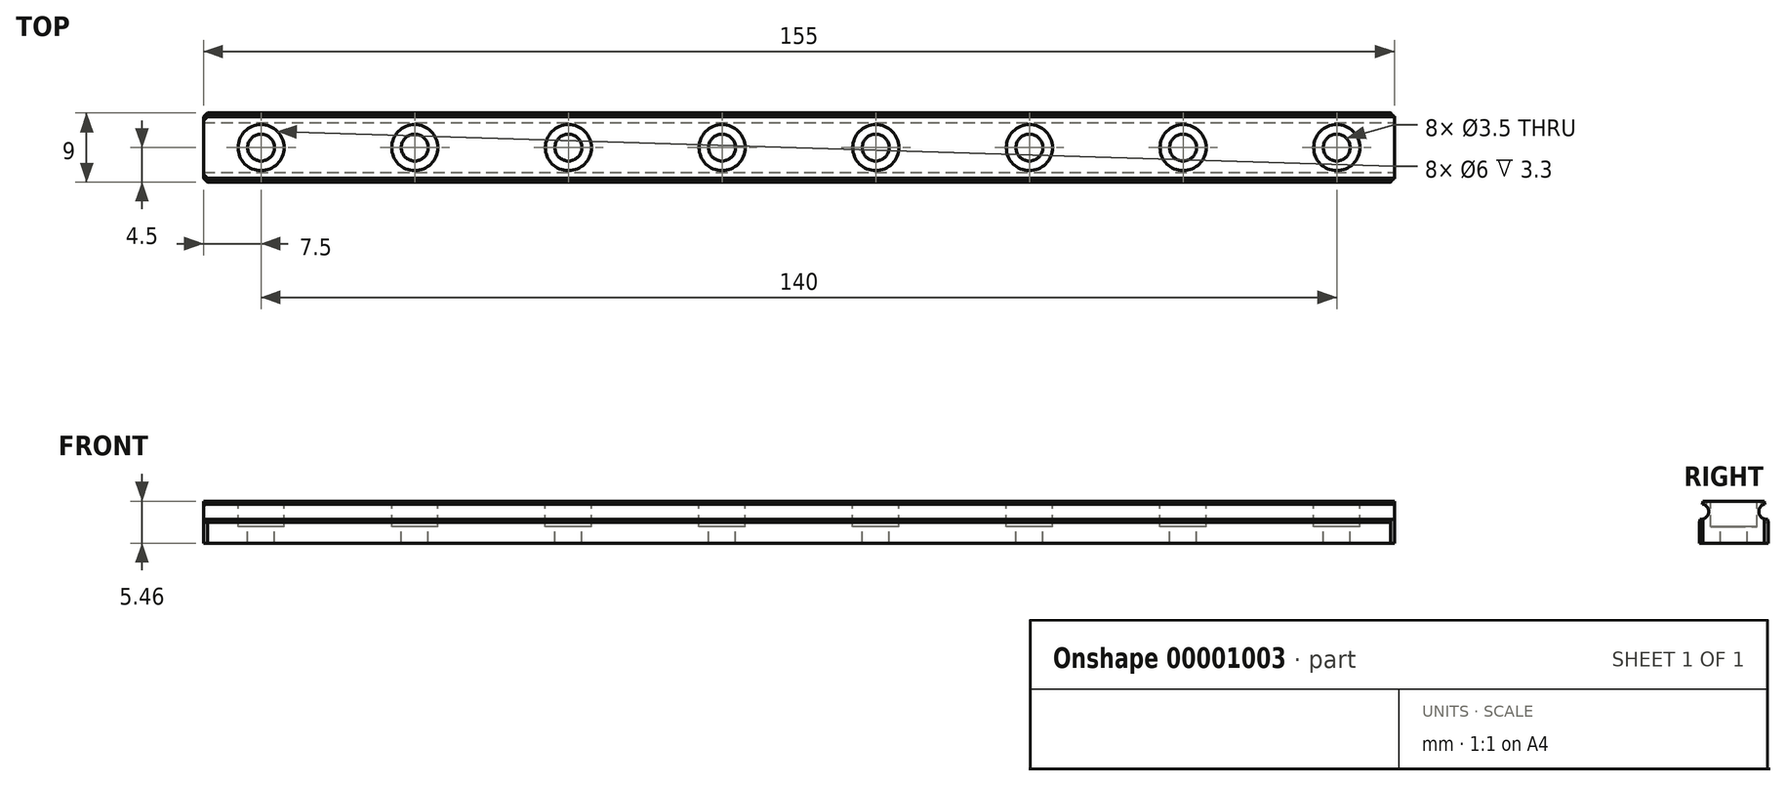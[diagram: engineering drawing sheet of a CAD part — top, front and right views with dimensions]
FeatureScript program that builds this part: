
annotation { "Feature Type Name" : "Feature", "Feature Type Description" : "" }
export const myFeature = defineFeature(function(context is Context, id is Id, definition is map)
    precondition{}
    {
        {
            var Q0;
            Q0=qCreatedBy(makeId("Top.planeOp"),FACE);
            var sketch = newSketch(context, id + "F0", { "sketchPlane" : qUnion([Q0])});
            skLineSegment(sketch, "E0.bottom", {"start": v(77.5, -4.5) * mm, "end": v(-77.5, -4.5) * mm});
            skLineSegment(sketch, "E0.top", {"start": v(77.5, 4.5) * mm, "end": v(-77.5, 4.5) * mm});
            skLineSegment(sketch, "E0.left", {"start": v(77.5, -4.5) * mm, "end": v(77.5, 4.5) * mm});
            skLineSegment(sketch, "E0.right", {"start": v(-77.5, -4.5) * mm, "end": v(-77.5, 4.5) * mm});
            skCircle(sketch, "E1", {"center": v(-10, 0) * mm, "radius": 1.75 * mm});
            skCircle(sketch, "E2", {"center": v(10, 0) * mm, "radius": 1.75 * mm});
            skCircle(sketch, "E3", {"center": v(30, 0) * mm, "radius": 1.75 * mm});
            skCircle(sketch, "E4", {"center": v(-30, 0) * mm, "radius": 1.75 * mm});
            skCircle(sketch, "E5", {"center": v(-50, 0) * mm, "radius": 1.75 * mm});
            skCircle(sketch, "E6", {"center": v(30, 0) * mm, "radius": 3 * mm});
            skCircle(sketch, "E7", {"center": v(10, 0) * mm, "radius": 3 * mm});
            skCircle(sketch, "E8", {"center": v(-10, 0) * mm, "radius": 3 * mm});
            skCircle(sketch, "E9", {"center": v(-30, 0) * mm, "radius": 3 * mm});
            skCircle(sketch, "E10", {"center": v(-50, 0) * mm, "radius": 3 * mm});
            skCircle(sketch, "E11", {"center": v(50, 0) * mm, "radius": 1.75 * mm});
            skCircle(sketch, "E12", {"center": v(50, 0) * mm, "radius": 3 * mm});
            skCircle(sketch, "E13", {"center": v(-70, 0) * mm, "radius": 1.75 * mm});
            skCircle(sketch, "E14", {"center": v(-70, 0) * mm, "radius": 3 * mm});
            skCircle(sketch, "E15", {"center": v(70, 0) * mm, "radius": 1.75 * mm});
            skCircle(sketch, "E16", {"center": v(70, 0) * mm, "radius": 3 * mm});
            skSolve(sketch);
        }
        {
            var Q0;
            Q0=makeQuery(id+"F0.imprint","IMPRINT",FACE,{"disambiguationData":[TD([[makeQuery(id+"F0.imprint","IMPRINT",EDGE,{"derivedFrom":sQuery(id+"F0.wireOp",EDGE,"E0.bottom")}),-1.0]])]});
            var Q1;
            Q1=makeQuery(id+"F0.imprint","IMPRINT",FACE,{"disambiguationData":[TD([[makeQuery(id+"F0.imprint","IMPRINT",EDGE,{"derivedFrom":sQuery(id+"F0.wireOp",EDGE,"E1")}),-1.0]])]});
            var Q2;
            Q2=makeQuery(id+"F0.imprint","IMPRINT",FACE,{"disambiguationData":[TD([[makeQuery(id+"F0.imprint","IMPRINT",EDGE,{"derivedFrom":sQuery(id+"F0.wireOp",EDGE,"E2")}),-1.0]])]});
            var Q3;
            Q3=makeQuery(id+"F0.imprint","IMPRINT",FACE,{"disambiguationData":[TD([[makeQuery(id+"F0.imprint","IMPRINT",EDGE,{"derivedFrom":sQuery(id+"F0.wireOp",EDGE,"E3")}),-1.0]])]});
            var Q4;
            Q4=makeQuery(id+"F0.imprint","IMPRINT",FACE,{"disambiguationData":[TD([[makeQuery(id+"F0.imprint","IMPRINT",EDGE,{"derivedFrom":sQuery(id+"F0.wireOp",EDGE,"E4")}),-1.0]])]});
            var Q5;
            Q5=makeQuery(id+"F0.imprint","IMPRINT",FACE,{"disambiguationData":[TD([[makeQuery(id+"F0.imprint","IMPRINT",EDGE,{"derivedFrom":sQuery(id+"F0.wireOp",EDGE,"E5")}),-1.0]])]});
            var Q6;
            Q6=makeQuery(id+"F0.imprint","IMPRINT",FACE,{"disambiguationData":[TD([[makeQuery(id+"F0.imprint","IMPRINT",EDGE,{"derivedFrom":sQuery(id+"F0.wireOp",EDGE,"E13")}),-1.0]])]});
            var Q7;
            Q7=makeQuery(id+"F0.imprint","IMPRINT",FACE,{"disambiguationData":[TD([[makeQuery(id+"F0.imprint","IMPRINT",EDGE,{"derivedFrom":sQuery(id+"F0.wireOp",EDGE,"E11")}),-1.0]])]});
            var Q8;
            Q8=makeQuery(id+"F0.imprint","IMPRINT",FACE,{"disambiguationData":[TD([[makeQuery(id+"F0.imprint","IMPRINT",EDGE,{"derivedFrom":sQuery(id+"F0.wireOp",EDGE,"E15")}),-1.0]])]});
            extrude(context, id + "F1", {"entities" : qUnion([Q0, Q1, Q2, Q3, Q4, Q5, Q6, Q7, Q8]), "oppositeDirection" : true, "depth" : 5.46 * mm});
        }
        {
            var Q0;
            Q0=makeQuery(id+"F0.imprint","IMPRINT",FACE,{"disambiguationData":[TD([[makeQuery(id+"F0.imprint","IMPRINT",EDGE,{"derivedFrom":sQuery(id+"F0.wireOp",EDGE,"E13")}),-1.0]])]});
            var Q1;
            Q1=makeQuery(id+"F0.imprint","IMPRINT",FACE,{"disambiguationData":[TD([[makeQuery(id+"F0.imprint","IMPRINT",EDGE,{"derivedFrom":sQuery(id+"F0.wireOp",EDGE,"E5")}),-1.0]])]});
            var Q2;
            Q2=makeQuery(id+"F0.imprint","IMPRINT",FACE,{"disambiguationData":[TD([[makeQuery(id+"F0.imprint","IMPRINT",EDGE,{"derivedFrom":sQuery(id+"F0.wireOp",EDGE,"E4")}),-1.0]])]});
            var Q3;
            Q3=makeQuery(id+"F0.imprint","IMPRINT",FACE,{"disambiguationData":[TD([[makeQuery(id+"F0.imprint","IMPRINT",EDGE,{"derivedFrom":sQuery(id+"F0.wireOp",EDGE,"E1")}),-1.0]])]});
            var Q4;
            Q4=makeQuery(id+"F0.imprint","IMPRINT",FACE,{"disambiguationData":[TD([[makeQuery(id+"F0.imprint","IMPRINT",EDGE,{"derivedFrom":sQuery(id+"F0.wireOp",EDGE,"E2")}),-1.0]])]});
            var Q5;
            Q5=makeQuery(id+"F0.imprint","IMPRINT",FACE,{"disambiguationData":[TD([[makeQuery(id+"F0.imprint","IMPRINT",EDGE,{"derivedFrom":sQuery(id+"F0.wireOp",EDGE,"E3")}),-1.0]])]});
            var Q6;
            Q6=makeQuery(id+"F0.imprint","IMPRINT",FACE,{"disambiguationData":[TD([[makeQuery(id+"F0.imprint","IMPRINT",EDGE,{"derivedFrom":sQuery(id+"F0.wireOp",EDGE,"E11")}),-1.0]])]});
            var Q7;
            Q7=makeQuery(id+"F0.imprint","IMPRINT",FACE,{"disambiguationData":[TD([[makeQuery(id+"F0.imprint","IMPRINT",EDGE,{"derivedFrom":sQuery(id+"F0.wireOp",EDGE,"E15")}),-1.0]])]});
            extrude(context, id + "F2", {"entities" : qUnion([Q0, Q1, Q2, Q3, Q4, Q5, Q6, Q7]), "operationType" : NewBodyOperationType.REMOVE, "oppositeDirection" : true, "depth" : 3.3 * mm});
        }
        {
            var Q0;
            Q0=makeQuery(id+"F1.opExtrude","SWEPT_FACE",FACE,{"disambiguationData":[OSD([sQuery(id+"F0.wireOp",EDGE,"E0.left")])]});
            var sketch = newSketch(context, id + "F3", { "sketchPlane" : qUnion([Q0])});
            skLineSegment(sketch, "E17", {"start": v(-4, 0) * mm, "end": v(-4.07, -0.38) * mm});
            skLineSegment(sketch, "E18", {"start": v(4.5, -2.73) * mm, "end": v(4.43, -2.35) * mm});
            skArc(sketch, "E19", {"start": v(-4.43, -2.35) * mm, "mid": v(-3.27, -1.55) * mm, "end": v(-4.07, -0.38) * mm});
            skArc(sketch, "E20", {"start": v(4.07, -0.38) * mm, "mid": v(3.27, -1.55) * mm, "end": v(4.43, -2.35) * mm});
            skLineSegment(sketch, "E21.trimOffspring", {"start": v(-4.43, -2.35) * mm, "end": v(-4.5, -2.73) * mm});
            skLineSegment(sketch, "E22.trimOffspring", {"start": v(4.07, -0.38) * mm, "end": v(4, 0) * mm});
            skLineSegment(sketch, "E23", {"start": v(-4, 0) * mm, "end": v(-4.5, 0) * mm});
            skLineSegment(sketch, "E24", {"start": v(-4.5, 0) * mm, "end": v(-4.5, -2.73) * mm});
            skLineSegment(sketch, "E25", {"start": v(4, 0) * mm, "end": v(4.5, 0) * mm});
            skLineSegment(sketch, "E26", {"start": v(4.5, 0) * mm, "end": v(4.5, -2.73) * mm});
            skSolve(sketch);
        }
        {
            var Q0;
            {Q0=qUnion([makeQuery(id+"F3.imprint","IMPRINT",FACE,{"disambiguationData":[TD([[makeQuery(id+"F3.imprint","IMPRINT",EDGE,{"derivedFrom":sQuery(id+"F3.wireOp",EDGE,"E17")}),-1.0]])]}),makeQuery(id+"F3.imprint","IMPRINT",FACE,{"disambiguationData":[TD([[makeQuery(id+"F3.imprint","IMPRINT",EDGE,{"derivedFrom":sQuery(id+"F3.wireOp",EDGE,"E18")}),-1.0]])]})]);}
            extrude(context, id + "F4", {"entities" : qUnion([Q0]), "operationType" : NewBodyOperationType.REMOVE, "endBound" : BoundingType.THROUGH_ALL, "oppositeDirection" : true, "depth" : 25.4 * mm});
        }
        {
            var Q0;
            Q0=makeQuery(id+"F4.boolean.opBoolean","COPY",EDGE,{"derivedFrom":makeQuery(id+"F4.opExtrude","CAP_EDGE",EDGE,{"disambiguationData":[OSD([sQuery(id+"F3.wireOp",EDGE,"E22.trimOffspring")])],"isStart":true})});
            var Q1;
            Q1=makeQuery(id+"F4.boolean.opBoolean","COPY",EDGE,{"derivedFrom":makeQuery(id+"F4.opExtrude","CAP_EDGE",EDGE,{"disambiguationData":[OSD([sQuery(id+"F3.wireOp",EDGE,"E18")])],"isStart":true})});
            var Q2;
            Q2=makeQuery(id+"F1.opExtrude","SWEPT_EDGE",EDGE,{"disambiguationData":[OSD([sQuery(id+"F0.wireOp",EDGE,"E0.top"),sQuery(id+"F0.wireOp",EDGE,"E0.left")])]});
            var Q3;
            Q3=makeQuery(id+"F1.opExtrude","SWEPT_EDGE",EDGE,{"disambiguationData":[OSD([sQuery(id+"F0.wireOp",EDGE,"E0.bottom"),sQuery(id+"F0.wireOp",EDGE,"E0.left")])]});
            var Q4;
            Q4=makeQuery(id+"F4.boolean.opBoolean","COPY",EDGE,{"derivedFrom":makeQuery(id+"F4.opExtrude","CAP_EDGE",EDGE,{"disambiguationData":[OSD([sQuery(id+"F3.wireOp",EDGE,"E21.trimOffspring")])],"isStart":true})});
            var Q5;
            Q5=makeQuery(id+"F4.boolean.opBoolean","COPY",EDGE,{"derivedFrom":makeQuery(id+"F4.opExtrude","CAP_EDGE",EDGE,{"disambiguationData":[OSD([sQuery(id+"F3.wireOp",EDGE,"E17")])],"isStart":true})});
            var Q6;
            Q6=makeQuery(id+"F1.opExtrude","SWEPT_EDGE",EDGE,{"disambiguationData":[OSD([sQuery(id+"F0.wireOp",EDGE,"E0.bottom"),sQuery(id+"F0.wireOp",EDGE,"E0.right")])]});
            var Q7;
            Q7=makeQuery(id+"F4.boolean.opBoolean","INTERSECT",EDGE,{"derivedFrom":[makeQuery(id+"F1.opExtrude","SWEPT_FACE",FACE,{"disambiguationData":[OSD([sQuery(id+"F0.wireOp",EDGE,"E0.right")])]}),makeQuery(id+"F4.opExtrude","SWEPT_FACE",FACE,{"disambiguationData":[OSD([sQuery(id+"F3.wireOp",EDGE,"E21.trimOffspring")])]})]});
            var Q8;
            Q8=makeQuery(id+"F4.boolean.opBoolean","INTERSECT",EDGE,{"derivedFrom":[makeQuery(id+"F1.opExtrude","SWEPT_FACE",FACE,{"disambiguationData":[OSD([sQuery(id+"F0.wireOp",EDGE,"E0.right")])]}),makeQuery(id+"F4.opExtrude","SWEPT_FACE",FACE,{"disambiguationData":[OSD([sQuery(id+"F3.wireOp",EDGE,"E17")])]})]});
            var Q9;
            Q9=makeQuery(id+"F4.boolean.opBoolean","INTERSECT",EDGE,{"derivedFrom":[makeQuery(id+"F1.opExtrude","SWEPT_FACE",FACE,{"disambiguationData":[OSD([sQuery(id+"F0.wireOp",EDGE,"E0.right")])]}),makeQuery(id+"F4.opExtrude","SWEPT_FACE",FACE,{"disambiguationData":[OSD([sQuery(id+"F3.wireOp",EDGE,"E22.trimOffspring")])]})]});
            var Q10;
            Q10=makeQuery(id+"F1.opExtrude","SWEPT_EDGE",EDGE,{"disambiguationData":[OSD([sQuery(id+"F0.wireOp",EDGE,"E0.top"),sQuery(id+"F0.wireOp",EDGE,"E0.right")])]});
            var Q11;
            Q11=makeQuery(id+"F4.boolean.opBoolean","INTERSECT",EDGE,{"derivedFrom":[makeQuery(id+"F1.opExtrude","SWEPT_FACE",FACE,{"disambiguationData":[OSD([sQuery(id+"F0.wireOp",EDGE,"E0.right")])]}),makeQuery(id+"F4.opExtrude","SWEPT_FACE",FACE,{"disambiguationData":[OSD([sQuery(id+"F3.wireOp",EDGE,"E18")])]})]});
            chamfer(context, id + "F5", {"entities" : qUnion([Q0, Q1, Q2, Q3, Q4, Q5, Q6, Q7, Q8, Q9, Q10, Q11]), "width" : 0.5 * mm, "tangentPropagation" : true});
        }
    });
